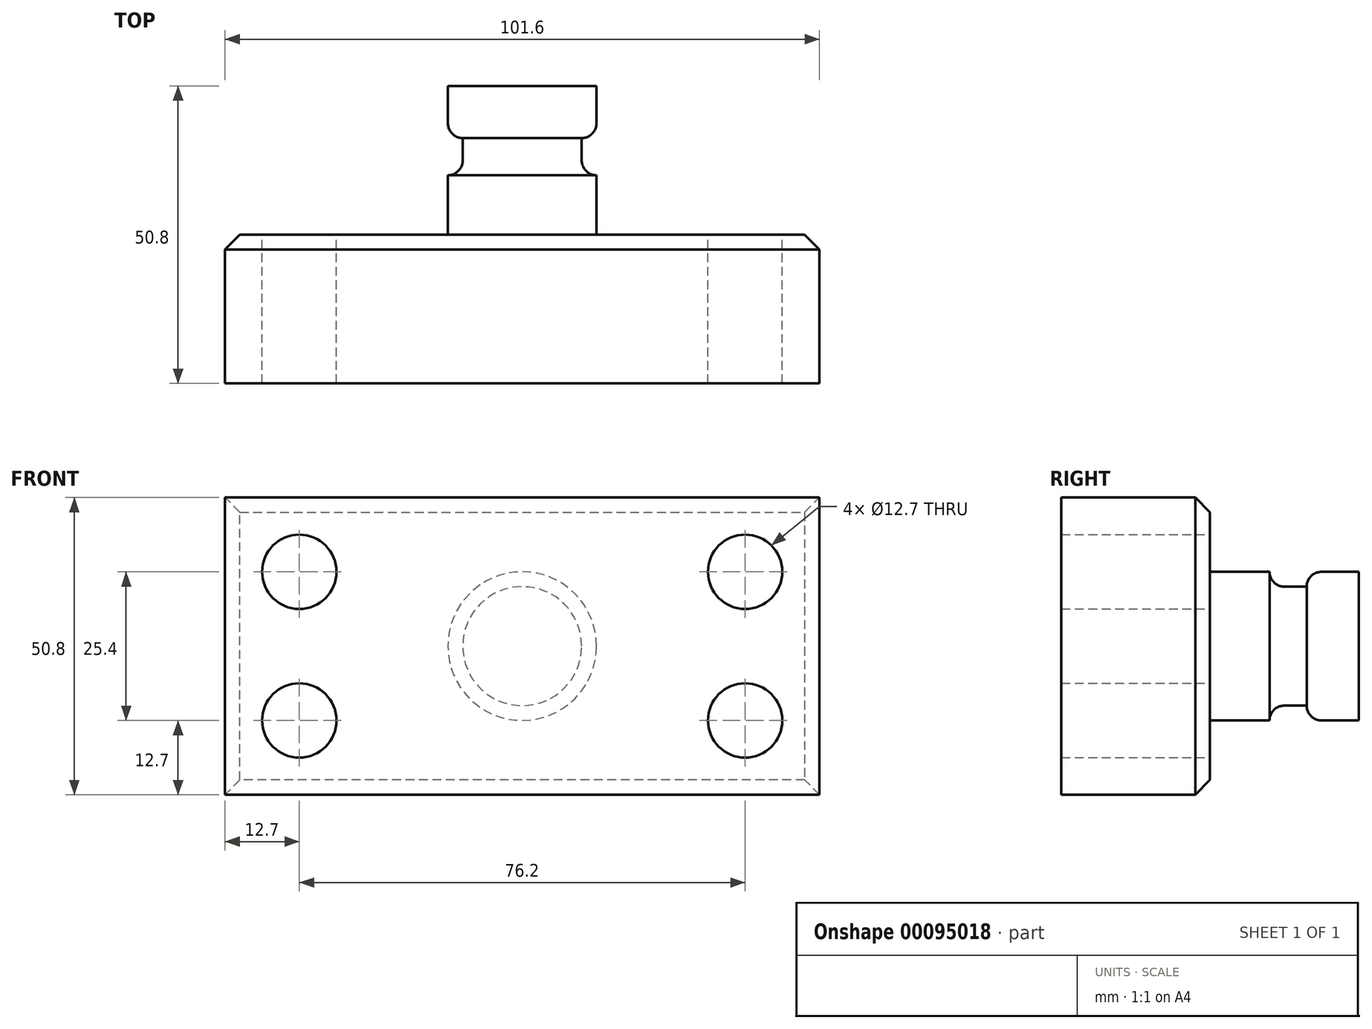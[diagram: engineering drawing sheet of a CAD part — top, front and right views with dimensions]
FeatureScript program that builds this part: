
annotation { "Feature Type Name" : "Feature", "Feature Type Description" : "" }
export const myFeature = defineFeature(function(context is Context, id is Id, definition is map)
    precondition{}
    {
        {
            var Q0;
            Q0=qCreatedBy(makeId("Front.planeOp"),FACE);
            var sketch = newSketch(context, id + "F0", { "sketchPlane" : qUnion([Q0])});
            skLineSegment(sketch, "E0.bottom", {"start": v(50.8, -25.4) * mm, "end": v(-50.8, -25.4) * mm});
            skLineSegment(sketch, "E0.top", {"start": v(50.8, 25.4) * mm, "end": v(-50.8, 25.4) * mm});
            skLineSegment(sketch, "E0.left", {"start": v(50.8, -25.4) * mm, "end": v(50.8, 25.4) * mm});
            skLineSegment(sketch, "E0.right", {"start": v(-50.8, -25.4) * mm, "end": v(-50.8, 25.4) * mm});
            skPoint(sketch, "E0.middle", {"position": v(0, 0) * mm});
            skSolve(sketch);
        }
        {
            var Q0;
            Q0 = qSketchRegion(id + "F0", true);
            extrude(context, id + "F1", {"entities" : qUnion([Q0]), "depth" : 25.4 * mm});
        }
        {
            var Q0;
            Q0=qCreatedBy(makeId("Front.planeOp"),FACE);
            var sketch = newSketch(context, id + "F2", { "sketchPlane" : qUnion([Q0])});
            skCircle(sketch, "E1", {"center": v(-38.1, 12.7) * mm, "radius": 6.35 * mm});
            skCircle(sketch, "E2", {"center": v(-38.1, -12.7) * mm, "radius": 6.35 * mm});
            skCircle(sketch, "E3", {"center": v(38.1, -12.7) * mm, "radius": 6.35 * mm});
            skCircle(sketch, "E4", {"center": v(38.1, 12.7) * mm, "radius": 6.35 * mm});
            skSolve(sketch);
        }
        {
            var Q0;
            Q0 = qSketchRegion(id + "F2", true);
            extrude(context, id + "F3", {"entities" : qUnion([Q0]), "operationType" : NewBodyOperationType.REMOVE, "endBound" : BoundingType.THROUGH_ALL, "depth" : 50.8 * mm});
        }
        {
            var Q0;
            Q0=qCreatedBy(makeId("Top.planeOp"),FACE);
            var sketch = newSketch(context, id + "F4", { "sketchPlane" : qUnion([Q0])});
            skLineSegment(sketch, "E5.bottom", {"start": v(0, 0) * mm, "end": v(12.7, 0) * mm});
            skLineSegment(sketch, "E5.top", {"start": v(0, 25.4) * mm, "end": v(12.7, 25.4) * mm});
            skLineSegment(sketch, "E5.left", {"start": v(0, 0) * mm, "end": v(0, 25.4) * mm});
            skLineSegment(sketch, "E5.right", {"start": v(12.7, 0) * mm, "end": v(12.7, 25.4) * mm});
            skSolve(sketch);
        }
        {
            var Q0;
            Q0=makeQuery(id+"F4.imprint","IMPRINT",FACE,{"disambiguationData":[TD([[makeQuery(id+"F4.imprint","IMPRINT",EDGE,{"derivedFrom":sQuery(id+"F4.wireOp",EDGE,"E5.bottom")}),1.0]])]});
            var Q1;
            Q1=sQuery(id+"F4.wireOp",EDGE,"E5.left");
            revolve(context, id + "F5", {"operationType" : NewBodyOperationType.ADD, "entities" : qUnion([Q0]), "axis" : qUnion([Q1]), "revolveType" : RevolveType.FULL});
        }
        {
            var Q0;
            Q0=qCreatedBy(makeId("Top.planeOp"),FACE);
            var sketch = newSketch(context, id + "F6", { "sketchPlane" : qUnion([Q0])});
            skLineSegment(sketch, "E6.bottom", {"start": v(-10.16, 16.51) * mm, "end": v(-19.15, 16.51) * mm});
            skLineSegment(sketch, "E6.top", {"start": v(-10.16, 10.16) * mm, "end": v(-19.15, 10.16) * mm});
            skLineSegment(sketch, "E6.left", {"start": v(-10.16, 16.51) * mm, "end": v(-10.16, 10.16) * mm});
            skLineSegment(sketch, "E6.right", {"start": v(-19.15, 16.51) * mm, "end": v(-19.15, 10.16) * mm});
            skLineSegment(sketch, "E7", {"start": v(0, 0) * mm, "end": v(0, 72.24) * mm, "construction": true});
            skLineSegment(sketch, "E8", {"start": v(0, 72.24) * mm, "end": v(0, -58.9) * mm, "construction": true});
            skSolve(sketch);
        }
        {
            var Q0;
            Q0 = qSketchRegion(id + "F6", true);
            var Q1;
            Q1=sQuery(id+"F6.wireOp",EDGE,"E8");
            revolve(context, id + "F7", {"operationType" : NewBodyOperationType.REMOVE, "entities" : qUnion([Q0]), "axis" : qUnion([Q1]), "revolveType" : RevolveType.FULL, "oppositeDirection" : true});
        }
        {
            var Q0;
            Q0=makeQuery(id+"F5.opRevolve","SWEPT_EDGE",EDGE,{"disambiguationData":[OSD([sQuery(id+"F4.wireOp",EDGE,"E5.bottom"),sQuery(id+"F4.wireOp",EDGE,"E5.right")])]});
            var Q1;
            Q1=makeQuery(id+"F7.boolean.opBoolean","COPY",EDGE,{"derivedFrom":makeQuery(id+"F7.opRevolve","SWEPT_EDGE",EDGE,{"disambiguationData":[OSD([sQuery(id+"F6.wireOp",EDGE,"E6.top"),sQuery(id+"F6.wireOp",EDGE,"E6.left")])]})});
            var Q2;
            Q2=makeQuery(id+"F7.boolean.opBoolean","INTERSECT",EDGE,{"derivedFrom":[makeQuery(id+"F5.opRevolve","SWEPT_FACE",FACE,{"disambiguationData":[OSD([sQuery(id+"F4.wireOp",EDGE,"E5.right")])]}),makeQuery(id+"F7.opRevolve","SWEPT_FACE",FACE,{"disambiguationData":[OSD([sQuery(id+"F6.wireOp",EDGE,"E6.bottom")])]})]});
            fillet(context, id + "F8", {"entities" : qUnion([Q0, Q1, Q2]), "radius" : 2.54 * mm, "tangentPropagation" : true, "allowEdgeOverflow" : false});
        }
        {
            var Q0;
            Q0=makeQuery(id+"F1.opExtrude","CAP_EDGE",EDGE,{"disambiguationData":[OSD([sQuery(id+"F0.wireOp",EDGE,"E0.top")])],"isStart":true});
            var Q1;
            Q1=makeQuery(id+"F1.opExtrude","CAP_EDGE",EDGE,{"disambiguationData":[OSD([sQuery(id+"F0.wireOp",EDGE,"E0.left")])],"isStart":true});
            var Q2;
            Q2=makeQuery(id+"F1.opExtrude","CAP_EDGE",EDGE,{"disambiguationData":[OSD([sQuery(id+"F0.wireOp",EDGE,"E0.bottom")])],"isStart":true});
            var Q3;
            Q3=makeQuery(id+"F1.opExtrude","CAP_EDGE",EDGE,{"disambiguationData":[OSD([sQuery(id+"F0.wireOp",EDGE,"E0.right")])],"isStart":true});
            chamfer(context, id + "F9", {"entities" : qUnion([Q0, Q1, Q2, Q3]), "width" : 2.54 * mm, "tangentPropagation" : true});
        }
    });
